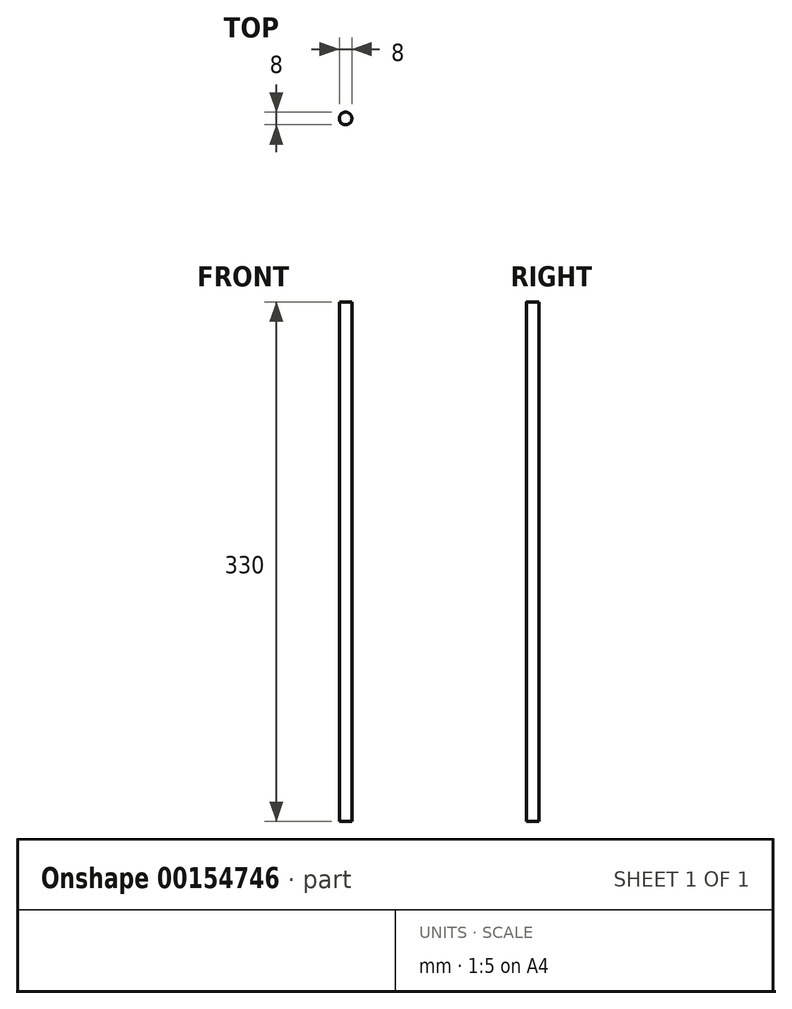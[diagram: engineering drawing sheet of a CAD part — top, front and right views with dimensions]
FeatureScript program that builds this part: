
annotation { "Feature Type Name" : "Feature", "Feature Type Description" : "" }
export const myFeature = defineFeature(function(context is Context, id is Id, definition is map)
    precondition{}
    {
        {
            var Q0;
            Q0=qCreatedBy(makeId("Top.planeOp"),FACE);
            var sketch = newSketch(context, id + "F0", { "sketchPlane" : qUnion([Q0])});
            skCircle(sketch, "E0", {"center": v(0, 0.15) * mm, "radius": 4 * mm});
            skSolve(sketch);
        }
        {
            var Q0;
            Q0 = qSketchRegion(id + "F0", true);
            extrude(context, id + "F1", {"entities" : qUnion([Q0]), "depth" : 330 * mm});
        }
    });
